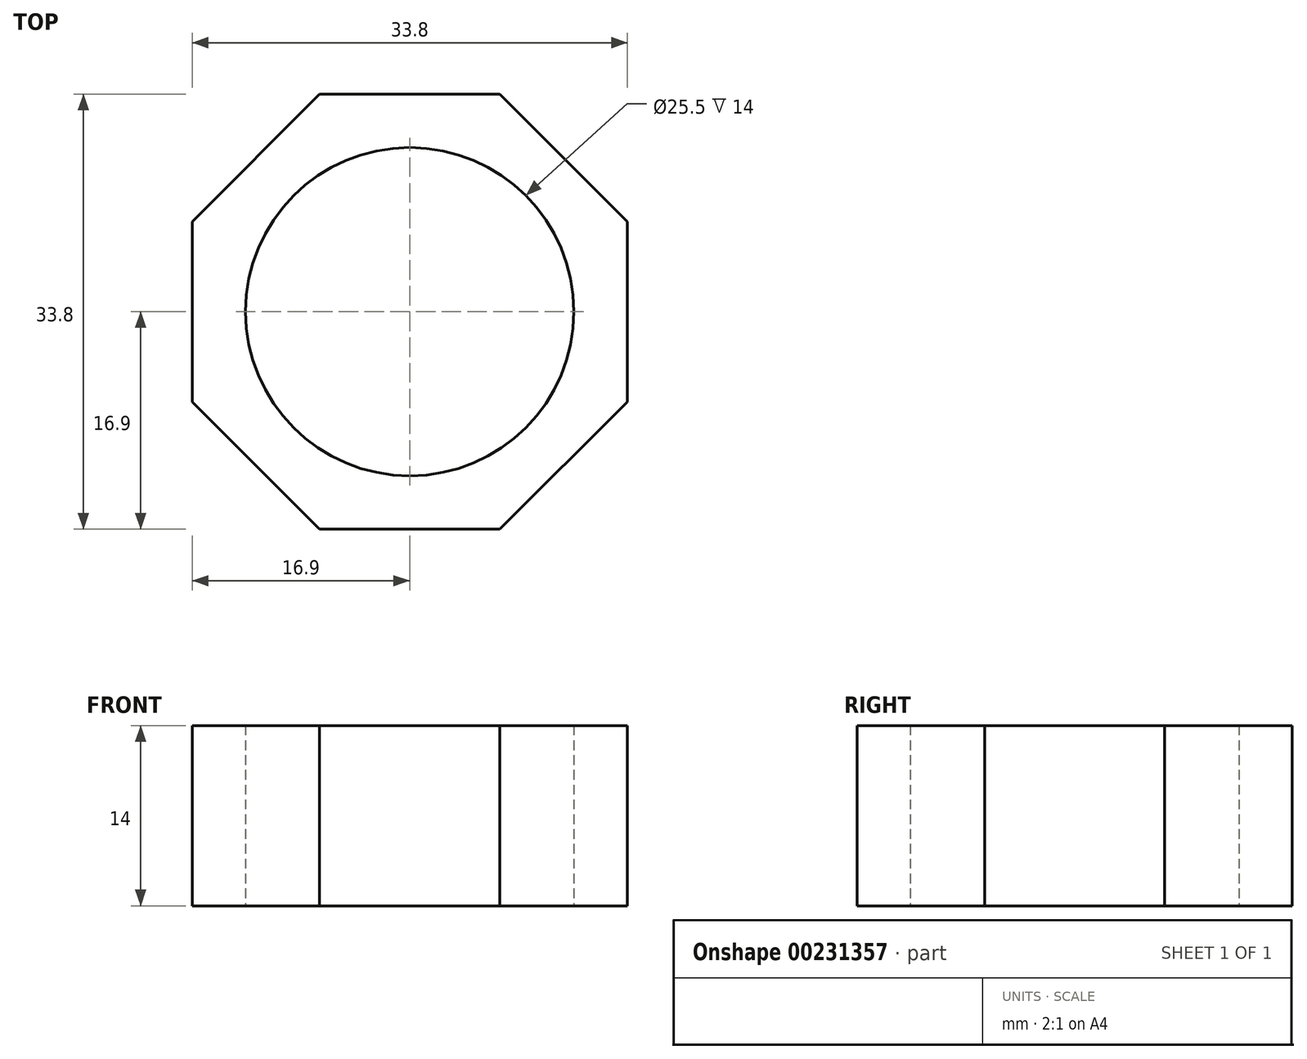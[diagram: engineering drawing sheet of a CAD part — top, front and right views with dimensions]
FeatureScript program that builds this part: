
annotation { "Feature Type Name" : "Feature", "Feature Type Description" : "" }
export const myFeature = defineFeature(function(context is Context, id is Id, definition is map)
    precondition{}
    {
        {
            var Q0;
            Q0=qCreatedBy(makeId("Top.planeOp"),FACE);
            var sketch = newSketch(context, id + "F0", { "sketchPlane" : qUnion([Q0])});
            skCircle(sketch, "E0", {"center": v(0, 0) * mm, "radius": 12.75 * mm});
            skCircle(sketch, "E1.cCircle", {"center": v(0, 0) * mm, "radius": 16.9 * mm, "construction": true});
            skLineSegment(sketch, "E1.0", {"start": v(-16.9, 7) * mm, "end": v(-7, 16.9) * mm});
            skLineSegment(sketch, "E1.1", {"start": v(-7, 16.9) * mm, "end": v(7, 16.9) * mm});
            skLineSegment(sketch, "E1.2", {"start": v(7, 16.9) * mm, "end": v(16.9, 7) * mm});
            skLineSegment(sketch, "E1.3", {"start": v(16.9, 7) * mm, "end": v(16.9, -7) * mm});
            skLineSegment(sketch, "E1.4", {"start": v(16.9, -7) * mm, "end": v(7, -16.9) * mm});
            skLineSegment(sketch, "E1.5", {"start": v(7, -16.9) * mm, "end": v(-7, -16.9) * mm});
            skLineSegment(sketch, "E1.6", {"start": v(-7, -16.9) * mm, "end": v(-16.9, -7) * mm});
            skLineSegment(sketch, "E1.7", {"start": v(-16.9, -7) * mm, "end": v(-16.9, 7) * mm});
            skPoint(sketch, "E1.0.midPoint", {"position": v(-11.95, 11.95) * mm});
            skSolve(sketch);
        }
        {
            var Q0;
            Q0 = qSketchRegion(id + "F0", true);
            extrude(context, id + "F1", {"entities" : qUnion([Q0]), "depth" : 14 * mm});
        }
    });
